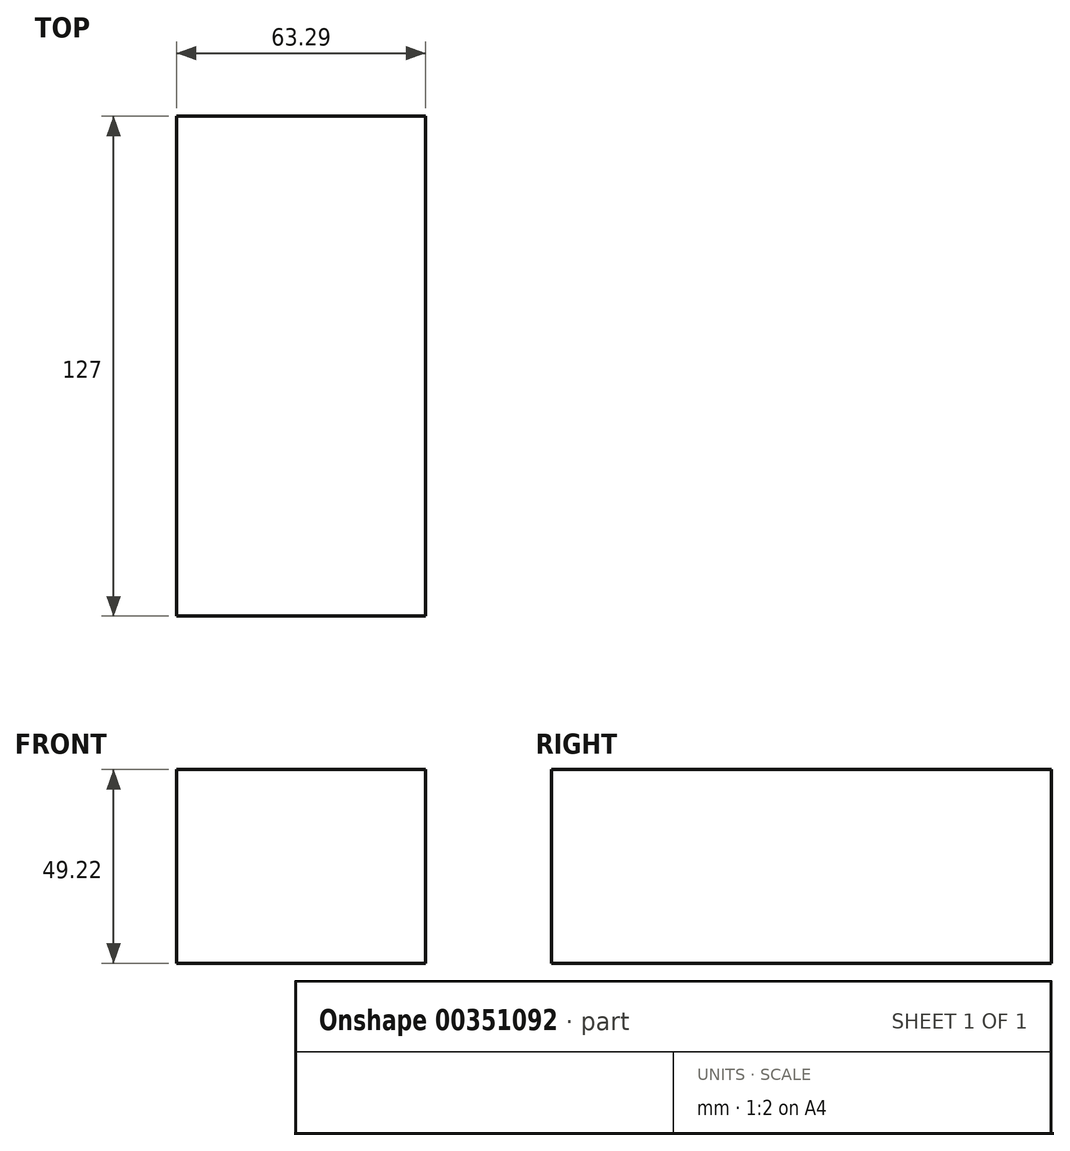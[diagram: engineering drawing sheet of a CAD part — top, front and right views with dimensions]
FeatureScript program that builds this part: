
annotation { "Feature Type Name" : "Feature", "Feature Type Description" : "" }
export const myFeature = defineFeature(function(context is Context, id is Id, definition is map)
    precondition{}
    {
        {
            var Q0;
            Q0=qCreatedBy(makeId("Front.planeOp"),FACE);
            var sketch = newSketch(context, id + "F0", { "sketchPlane" : qUnion([Q0])});
            skLineSegment(sketch, "E0.bottom", {"start": v(9.38, -15.53) * mm, "end": v(-53.91, -15.53) * mm});
            skLineSegment(sketch, "E0.top", {"start": v(9.38, 33.7) * mm, "end": v(-53.91, 33.7) * mm});
            skLineSegment(sketch, "E0.left", {"start": v(9.38, -15.53) * mm, "end": v(9.38, 33.7) * mm});
            skLineSegment(sketch, "E0.right", {"start": v(-53.91, -15.53) * mm, "end": v(-53.91, 33.7) * mm});
            skPoint(sketch, "E0.middle", {"position": v(-22.27, 9.08) * mm});
            skSolve(sketch);
        }
        {
            var Q0;
            Q0 = qSketchRegion(id + "F0", true);
            extrude(context, id + "F1", {"entities" : qUnion([Q0]), "endBound" : BoundingType.SYMMETRIC, "depth" : 127 * mm});
        }
    });
